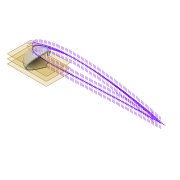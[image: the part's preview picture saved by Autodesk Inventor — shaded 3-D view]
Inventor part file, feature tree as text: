
AUTODESK INVENTOR PART (.ipt)
format: ipt  version: 2022 (Build 260153000, 153)  size: 451,584 bytes
history: native  units: mm
features: extrude x6, sketch x6, projected_geometry x4, plane x3, shell x1, revolve x1, fillet x1
ambient origin geometry x8: Origin, YZ Plane, XZ Plane, XY Plane, X Axis, Y Axis, Z Axis, Center Point
bodies: Solid1 (feature_tree)
feature tree (22):
  extrude  "Extrusion1"  Depth=2.0mm
  shell  "Shell1"  Thickness=80.0mm
  extrude  "Extrusion16"  Depth=12.217305mm
  revolve  "Revolution2"  [1 undecoded]
  extrude  "Extrusion17"  Depth=100.0mm TaperAngle=0.0deg
  plane  "Work Plane4"
  plane  "Work Plane5"
  plane  "Work Plane6"
  sketch  "Sketch41"  dims[d173=4.0mm d174=13.1mm d175=0.0mm]
  extrude  "Extrusion18"  Depth=13.1mm TaperAngle=0.0deg
  extrude  "Extrusion19"  Depth=100.0mm TaperAngle=0.0deg
  extrude  "Extrusion20"  Depth=1.5mm
  fillet  "Fillet5"  [1 undecoded]
  sketch  "Sketch3"  dims[d0=1.0mm d1=0.0mm d2=2.0mm d159=80.0mm]
  sketch  "Sketch37"  dims[d160=10.0mm d161=0.0mm d163=12.217305mm]
  sketch  "Sketch39"  dims[d164=1.0mm d165=0.0mm d166=6.454mm d167=16.2mm d168=-16.2mm]
  projected_geometry  "Projected Loop21"
  sketch  "Sketch40"  dims[d169=33.2mm d170=100.0mm d171=0.0mm]
  projected_geometry  "Projected Loop22"
  sketch  "Sketch42"  dims[d176=36.0mm d177=100.0mm d178=0.0mm d187=1.5mm]
  projected_geometry  "Project Cut Edges1"
  projected_geometry  "Project Cut Edges2"
note: 2 required parameter values undecoded (feature->parameter linkage not recoverable at this tier; creation-order binding heuristic only, values carry confidence <= 0.55)